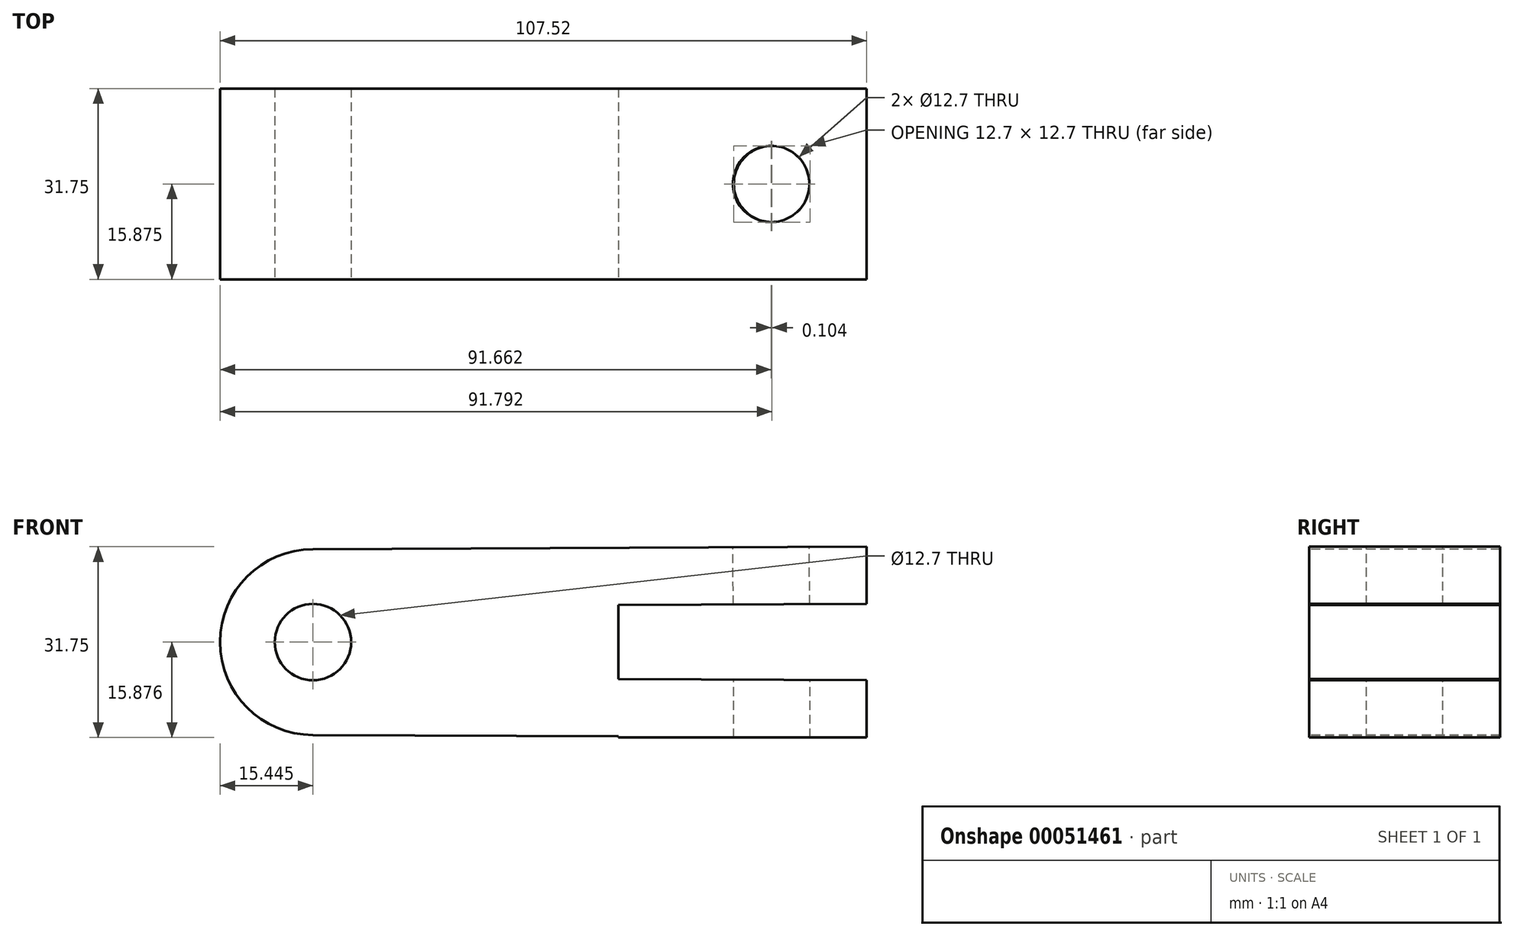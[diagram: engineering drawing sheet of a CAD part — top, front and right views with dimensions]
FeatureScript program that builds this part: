
annotation { "Feature Type Name" : "Feature", "Feature Type Description" : "" }
export const myFeature = defineFeature(function(context is Context, id is Id, definition is map)
    precondition{}
    {
        {
            var Q0;
            Q0=qCreatedBy(makeId("Front.planeOp"),FACE);
            var sketch = newSketch(context, id + "F0", { "sketchPlane" : qUnion([Q0])});
            skLineSegment(sketch, "E0.bottom", {"start": v(-52.83, 11.4) * mm, "end": v(55.12, 11.4) * mm});
            skLineSegment(sketch, "E0.top", {"start": v(-52.83, -20.35) * mm, "end": v(55.12, -20.35) * mm});
            skLineSegment(sketch, "E0.left", {"start": v(-52.83, 11.4) * mm, "end": v(-52.83, -20.35) * mm});
            skLineSegment(sketch, "E0.right", {"start": v(55.12, 11.4) * mm, "end": v(55.12, -20.35) * mm});
            skSolve(sketch);
        }
        {
            var Q0;
            Q0 = qSketchRegion(id + "F0", true);
            extrude(context, id + "F1", {"entities" : qUnion([Q0]), "depth" : 31.75 * mm});
        }
        {
            var Q0;
            Q0=makeQuery(id+"F1.opExtrude","CAP_FACE",FACE,{"disambiguationData":[OSD([sQuery(id+"F0.wireOp",EDGE,"E0.bottom"),sQuery(id+"F0.wireOp",EDGE,"E0.top"),sQuery(id+"F0.wireOp",EDGE,"E0.left"),sQuery(id+"F0.wireOp",EDGE,"E0.right")])],"isStart":false});
            var sketch = newSketch(context, id + "F2", { "sketchPlane" : qUnion([Q0])});
            skLineSegment(sketch, "E1.0", {"start": v(-36.96, 11.4) * mm, "end": v(-36.96, -20.35) * mm, "construction": true});
            skCircle(sketch, "E2", {"center": v(-36.96, -4.47) * mm, "radius": 6.35 * mm});
            skArc(sketch, "E3", {"start": v(-36.96, 10.97) * mm, "mid": v(-52.4, -4.47) * mm, "end": v(-36.96, -19.92) * mm});
            skLineSegment(sketch, "E4", {"start": v(-36.96, 10.97) * mm, "end": v(55.12, 11.4) * mm});
            skLineSegment(sketch, "E5", {"start": v(55.12, 11.4) * mm, "end": v(55.12, -20.35) * mm});
            skLineSegment(sketch, "E6", {"start": v(55.12, -20.35) * mm, "end": v(-36.96, -19.92) * mm});
            skLineSegment(sketch, "E7.0", {"start": v(-36.91, 1.45) * mm, "end": v(-34.69, 1.46) * mm});
            skLineSegment(sketch, "E8.0", {"start": v(55.16, -10.82) * mm, "end": v(13.84, -10.63) * mm});
            skLineSegment(sketch, "E9.trimOffspring", {"start": v(13.84, 1.68) * mm, "end": v(55.16, 1.88) * mm});
            skLineSegment(sketch, "E10.trimOffspring", {"start": v(-34.69, -10.4) * mm, "end": v(-36.91, -10.4) * mm});
            skLineSegment(sketch, "E11.trimOffspring", {"start": v(13.84, 1.68) * mm, "end": v(13.84, -10.63) * mm});
            skLineSegment(sketch, "E12.trimOffspring", {"start": v(13.84, -20.16) * mm, "end": v(13.84, -20.35) * mm});
            skSolve(sketch);
        }
        {
            var Q0;
            {var subQ2=sQuery(id+"F2.wireOp",EDGE,"E3");Q0=makeQuery(id+"F2.imprint","IMPRINT",FACE,{"disambiguationData":[TD([[makeQuery(id+"F2.imprint","IMPRINT",EDGE,{"derivedFrom":subQ2}),-1.0]])]});}
            var Q1;
            {var subQ5=sQuery(id+"F2.wireOp",EDGE,"E11.trimOffspring");Q1=makeQuery(id+"F2.imprint","IMPRINT",FACE,{"disambiguationData":[TD([[makeQuery(id+"F2.imprint","IMPRINT",EDGE,{"derivedFrom":subQ5}),1.0]])]});}
            var Q2;
            {var subQ0=sQuery(id+"F2.wireOp",EDGE,"E2");var subQ1=makeQuery(id+"F2.imprint","IMPRINT",VERTEX,{"disambiguationData":[OD(0.0)],"derivedFrom":subQ0});Q2=makeQuery(id+"F2.imprint","IMPRINT",FACE,{"disambiguationData":[TD([[makeQuery(id+"F2.imprint","IMPRINT",EDGE,{"disambiguationData":[TD([[subQ1,-1.0]])],"derivedFrom":subQ0}),1.0]])]});}
            extrude(context, id + "F3", {"entities" : qUnion([Q0, Q1, Q2]), "operationType" : NewBodyOperationType.REMOVE, "endBound" : BoundingType.THROUGH_ALL, "oppositeDirection" : true, "depth" : 25.4 * mm});
        }
        {
            var Q0;
            Q0=makeQuery(id+"F3.boolean.opBoolean","COPY",FACE,{"derivedFrom":makeQuery(id+"F3.opExtrude","SWEPT_FACE",FACE,{"disambiguationData":[OSD([sQuery(id+"F2.wireOp",EDGE,"E4")])]})});
            var sketch = newSketch(context, id + "F4", { "sketchPlane" : qUnion([Q0])});
            skLineSegment(sketch, "E13.0", {"start": v(39.3, -31.75) * mm, "end": v(39.3, -22.23) * mm, "construction": true});
            skCircle(sketch, "E14", {"center": v(39.3, -15.88) * mm, "radius": 6.35 * mm});
            skArc(sketch, "E15", {"start": v(39.3, -31.66) * mm, "mid": v(55.09, -15.88) * mm, "end": v(39.3, -0.09) * mm});
            skLineSegment(sketch, "E16", {"start": v(39.3, 0) * mm, "end": v(-36.9, 0) * mm});
            skLineSegment(sketch, "E17", {"start": v(-36.9, 0) * mm, "end": v(-36.9, -31.75) * mm});
            skLineSegment(sketch, "E18", {"start": v(-36.9, -31.75) * mm, "end": v(39.3, -31.66) * mm});
            skLineSegment(sketch, "E19.trimOffspring", {"start": v(39.3, -9.52) * mm, "end": v(39.3, 0) * mm, "construction": true});
            skLineSegment(sketch, "E20.0", {"start": v(4.37, -31.7) * mm, "end": v(4.37, -31.75) * mm});
            skLineSegment(sketch, "E21.0", {"start": v(0, -9.53) * mm, "end": v(-36.9, -9.53) * mm});
            skLineSegment(sketch, "E22.0", {"start": v(-36.91, -22.23) * mm, "end": v(0, -22.18) * mm});
            skLineSegment(sketch, "E23", {"start": v(0, -9.53) * mm, "end": v(0, -22.18) * mm});
            skLineSegment(sketch, "E24.trimOffspring", {"start": v(0, -31.7) * mm, "end": v(0, -31.75) * mm});
            skLineSegment(sketch, "E25.trimOffspring", {"start": v(38.26, -22.14) * mm, "end": v(39.29, -22.14) * mm});
            skSolve(sketch);
        }
        {
            var Q0;
            Q0=makeQuery(id+"F4.imprint","IMPRINT",FACE,{"disambiguationData":[TD([[makeQuery(id+"F4.imprint","IMPRINT",EDGE,{"derivedFrom":sQuery(id+"F4.wireOp",EDGE,"E14")}),1.0]])]});
            extrude(context, id + "F5", {"entities" : qUnion([Q0]), "operationType" : NewBodyOperationType.REMOVE, "endBound" : BoundingType.THROUGH_ALL, "oppositeDirection" : true, "depth" : 25.4 * mm});
        }
    });
